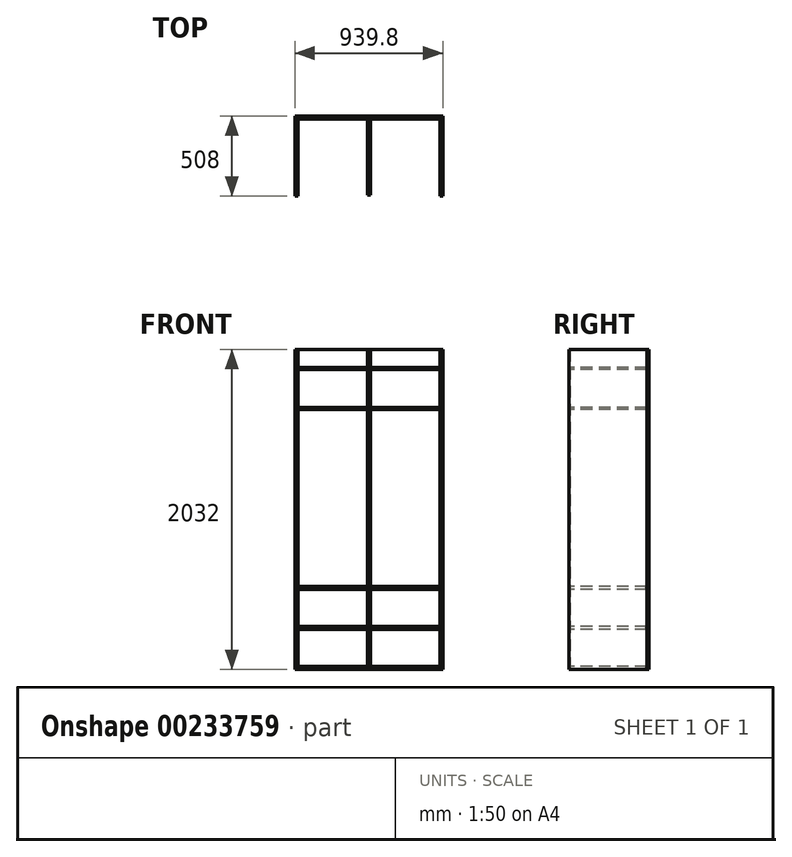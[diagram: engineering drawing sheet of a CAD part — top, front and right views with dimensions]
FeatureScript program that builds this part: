
annotation { "Feature Type Name" : "Feature", "Feature Type Description" : "" }
export const myFeature = defineFeature(function(context is Context, id is Id, definition is map)
    precondition{}
    {
        {
            var Q0;
            Q0=qCreatedBy(makeId("Front.planeOp"),FACE);
            var sketch = newSketch(context, id + "F0", { "sketchPlane" : qUnion([Q0])});
            skLineSegment(sketch, "E0.bottom", {"start": v(0, 0) * mm, "end": v(939.8, 0) * mm});
            skLineSegment(sketch, "E0.top", {"start": v(0, 2032) * mm, "end": v(939.8, 2032) * mm});
            skLineSegment(sketch, "E0.left", {"start": v(0, 0) * mm, "end": v(0, 2032) * mm});
            skLineSegment(sketch, "E0.right", {"start": v(939.8, 0) * mm, "end": v(939.8, 2032) * mm});
            skSolve(sketch);
        }
        {
            var Q0;
            Q0=makeQuery(id+"F0.imprint","IMPRINT",FACE,{"disambiguationData":[TD([[makeQuery(id+"F0.imprint","IMPRINT",EDGE,{"derivedFrom":sQuery(id+"F0.wireOp",EDGE,"E0.bottom")}),1.0]])]});
            extrude(context, id + "F1", {"entities" : qUnion([Q0]), "depth" : 19.05 * mm});
        }
        {
            var Q0;
            Q0=makeQuery(id+"F1.opExtrude","CAP_FACE",FACE,{"disambiguationData":[OSD([sQuery(id+"F0.wireOp",EDGE,"E0.bottom"),sQuery(id+"F0.wireOp",EDGE,"E0.top"),sQuery(id+"F0.wireOp",EDGE,"E0.left"),sQuery(id+"F0.wireOp",EDGE,"E0.right")])],"isStart":false});
            var sketch = newSketch(context, id + "F2", { "sketchPlane" : qUnion([Q0])});
            skLineSegment(sketch, "E1.bottom", {"start": v(0, 2032) * mm, "end": v(19.05, 2032) * mm});
            skLineSegment(sketch, "E1.top", {"start": v(0, 0) * mm, "end": v(19.05, 0) * mm});
            skLineSegment(sketch, "E1.left", {"start": v(0, 2032) * mm, "end": v(0, 0) * mm});
            skLineSegment(sketch, "E1.right", {"start": v(19.05, 2032) * mm, "end": v(19.05, 0) * mm});
            skLineSegment(sketch, "E2.bottom", {"start": v(939.8, 2032) * mm, "end": v(920.75, 2032) * mm});
            skLineSegment(sketch, "E2.top", {"start": v(939.8, 0) * mm, "end": v(920.75, 0) * mm});
            skLineSegment(sketch, "E2.left", {"start": v(939.8, 2032) * mm, "end": v(939.8, 0) * mm});
            skLineSegment(sketch, "E2.right", {"start": v(920.75, 2032) * mm, "end": v(920.75, 0) * mm});
            skLineSegment(sketch, "E3.bottom", {"start": v(469.9, 2032) * mm, "end": v(479.42, 2032) * mm});
            skLineSegment(sketch, "E3.top", {"start": v(469.9, 0) * mm, "end": v(479.42, 0) * mm});
            skLineSegment(sketch, "E3.right", {"start": v(479.42, 2032) * mm, "end": v(479.42, 0) * mm});
            skLineSegment(sketch, "E4.bottom", {"start": v(469.9, 2032) * mm, "end": v(460.37, 2032) * mm});
            skLineSegment(sketch, "E4.top", {"start": v(469.9, 0) * mm, "end": v(460.37, 0) * mm});
            skLineSegment(sketch, "E4.right", {"start": v(460.37, 2032) * mm, "end": v(460.37, 0) * mm});
            skSolve(sketch);
        }
        {
            var Q0;
            Q0 = qSketchRegion(id + "F2", true);
            extrude(context, id + "F3", {"entities" : qUnion([Q0]), "operationType" : NewBodyOperationType.REMOVE, "oppositeDirection" : true, "depth" : 6.35 * mm});
        }
        {
            var Q0;
            Q0=makeQuery(id+"F1.opExtrude","SWEPT_FACE",FACE,{"disambiguationData":[OSD([sQuery(id+"F0.wireOp",EDGE,"E0.right")])]});
            var sketch = newSketch(context, id + "F4", { "sketchPlane" : qUnion([Q0])});
            skLineSegment(sketch, "E5.bottom", {"start": v(-12.7, 2032) * mm, "end": v(-508, 2032) * mm});
            skLineSegment(sketch, "E5.top", {"start": v(-12.7, 0) * mm, "end": v(-508, 0) * mm});
            skLineSegment(sketch, "E5.left", {"start": v(-12.7, 2032) * mm, "end": v(-12.7, 0) * mm});
            skLineSegment(sketch, "E5.right", {"start": v(-508, 2032) * mm, "end": v(-508, 0) * mm});
            skSolve(sketch);
        }
        {
            var Q0;
            Q0=makeQuery(id+"F4.imprint","IMPRINT",FACE,{"disambiguationData":[TD([[makeQuery(id+"F4.imprint","IMPRINT",EDGE,{"derivedFrom":sQuery(id+"F4.wireOp",EDGE,"E5.bottom")}),1.0]])]});
            extrude(context, id + "F5", {"entities" : qUnion([Q0]), "oppositeDirection" : true, "depth" : 19.08 * mm});
        }
        {
            var Q0;
            Q0=makeQuery(id+"F1.opExtrude","SWEPT_FACE",FACE,{"disambiguationData":[OSD([sQuery(id+"F0.wireOp",EDGE,"E0.left")])]});
            var sketch = newSketch(context, id + "F6", { "sketchPlane" : qUnion([Q0])});
            skLineSegment(sketch, "E6.bottom", {"start": v(12.7, 2032) * mm, "end": v(508, 2032) * mm});
            skLineSegment(sketch, "E6.top", {"start": v(12.7, 0) * mm, "end": v(508, 0) * mm});
            skLineSegment(sketch, "E6.left", {"start": v(12.7, 2032) * mm, "end": v(12.7, 0) * mm});
            skLineSegment(sketch, "E6.right", {"start": v(508, 2032) * mm, "end": v(508, 0) * mm});
            skSolve(sketch);
        }
        {
            var Q0;
            Q0=makeQuery(id+"F6.imprint","IMPRINT",FACE,{"disambiguationData":[TD([[makeQuery(id+"F6.imprint","IMPRINT",EDGE,{"derivedFrom":sQuery(id+"F6.wireOp",EDGE,"E6.bottom")}),-1.0]])]});
            extrude(context, id + "F7", {"entities" : qUnion([Q0]), "oppositeDirection" : true, "depth" : 19.05 * mm});
        }
        {
            var Q0;
            Q0=makeQuery(id+"F3.boolean.opBoolean","COPY",FACE,{"derivedFrom":makeQuery(id+"F3.opExtrude","SWEPT_FACE",FACE,{"disambiguationData":[OSD([sQuery(id+"F2.wireOp",EDGE,"E3.right")])]})});
            var sketch = newSketch(context, id + "F8", { "sketchPlane" : qUnion([Q0])});
            skLineSegment(sketch, "E7.bottom", {"start": v(12.7, 2032) * mm, "end": v(501.65, 2032) * mm});
            skLineSegment(sketch, "E7.top", {"start": v(12.7, 0) * mm, "end": v(501.65, 0) * mm});
            skLineSegment(sketch, "E7.left", {"start": v(12.7, 2032) * mm, "end": v(12.7, 0) * mm});
            skLineSegment(sketch, "E7.right", {"start": v(501.65, 2032) * mm, "end": v(501.65, 0) * mm});
            skSolve(sketch);
        }
        {
            var Q0;
            Q0 = qSketchRegion(id + "F8", true);
            extrude(context, id + "F9", {"entities" : qUnion([Q0]), "depth" : 19.05 * mm});
        }
        {
            var Q0;
            {var subQ0=sQuery(id+"F0.wireOp",EDGE,"E0.bottom");var subQ1=sQuery(id+"F0.wireOp",EDGE,"E0.top");Q0=makeQuery(id+"F3.boolean.opBoolean","SPLIT",FACE,{"disambiguationData":[TD([makeQuery(id+"F3.opExtrude","SWEPT_FACE",FACE,{"disambiguationData":[OSD([sQuery(id+"F2.wireOp",EDGE,"E2.right")])]})])],"derivedFrom":makeQuery(id+"F1.opExtrude","CAP_FACE",FACE,{"disambiguationData":[OSD([subQ0,subQ1,sQuery(id+"F0.wireOp",EDGE,"E0.left"),sQuery(id+"F0.wireOp",EDGE,"E0.right")])],"isStart":false})});}
            var sketch = newSketch(context, id + "F10", { "sketchPlane" : qUnion([Q0])});
            skLineSegment(sketch, "E8.bottom", {"start": v(19.05, 0) * mm, "end": v(920.75, 0) * mm});
            skLineSegment(sketch, "E8.top", {"start": v(19.05, 19.05) * mm, "end": v(920.75, 19.05) * mm});
            skLineSegment(sketch, "E8.left", {"start": v(19.05, 0) * mm, "end": v(19.05, 19.05) * mm});
            skLineSegment(sketch, "E8.right", {"start": v(920.75, 0) * mm, "end": v(920.75, 19.05) * mm});
            skLineSegment(sketch, "E9.bottom", {"start": v(19.05, 254) * mm, "end": v(920.75, 254) * mm});
            skLineSegment(sketch, "E9.top", {"start": v(19.05, 273.05) * mm, "end": v(920.75, 273.05) * mm});
            skLineSegment(sketch, "E9.left", {"start": v(19.05, 254) * mm, "end": v(19.05, 273.05) * mm});
            skLineSegment(sketch, "E9.right", {"start": v(920.75, 254) * mm, "end": v(920.75, 273.05) * mm});
            skLineSegment(sketch, "E10.bottom", {"start": v(19.05, 508) * mm, "end": v(920.75, 508) * mm});
            skLineSegment(sketch, "E10.top", {"start": v(19.05, 527.05) * mm, "end": v(920.75, 527.05) * mm});
            skLineSegment(sketch, "E10.left", {"start": v(19.05, 508) * mm, "end": v(19.05, 527.05) * mm});
            skLineSegment(sketch, "E10.right", {"start": v(920.75, 508) * mm, "end": v(920.75, 527.05) * mm});
            skLineSegment(sketch, "E11.bottom", {"start": v(19.05, 1651) * mm, "end": v(920.75, 1651) * mm});
            skLineSegment(sketch, "E11.top", {"start": v(19.05, 1663.7) * mm, "end": v(920.75, 1663.7) * mm});
            skLineSegment(sketch, "E11.left", {"start": v(19.05, 1651) * mm, "end": v(19.05, 1663.7) * mm});
            skLineSegment(sketch, "E11.right", {"start": v(920.75, 1651) * mm, "end": v(920.75, 1663.7) * mm});
            skLineSegment(sketch, "E12.bottom", {"start": v(19.05, 1905) * mm, "end": v(920.75, 1905) * mm});
            skLineSegment(sketch, "E12.top", {"start": v(19.05, 1917.7) * mm, "end": v(920.75, 1917.7) * mm});
            skLineSegment(sketch, "E12.left", {"start": v(19.05, 1905) * mm, "end": v(19.05, 1917.7) * mm});
            skLineSegment(sketch, "E12.right", {"start": v(920.75, 1905) * mm, "end": v(920.75, 1917.7) * mm});
            skSolve(sketch);
        }
        {
            var Q0;
            Q0 = qSketchRegion(id + "F10", true);
            extrude(context, id + "F11", {"entities" : qUnion([Q0]), "operationType" : NewBodyOperationType.REMOVE, "oppositeDirection" : true, "depth" : 6.35 * mm});
        }
        {
            var Q0;
            Q0=makeQuery(id+"F7.opExtrude","CAP_FACE",FACE,{"disambiguationData":[OSD([sQuery(id+"F6.wireOp",EDGE,"E6.bottom"),sQuery(id+"F6.wireOp",EDGE,"E6.top"),sQuery(id+"F6.wireOp",EDGE,"E6.left"),sQuery(id+"F6.wireOp",EDGE,"E6.right")])],"isStart":false});
            var sketch = newSketch(context, id + "F12", { "sketchPlane" : qUnion([Q0])});
            skLineSegment(sketch, "E13.bottom", {"start": v(-12.7, 254) * mm, "end": v(-508, 254) * mm});
            skLineSegment(sketch, "E13.top", {"start": v(-12.7, 273.05) * mm, "end": v(-508, 273.05) * mm});
            skLineSegment(sketch, "E13.left", {"start": v(-12.7, 254) * mm, "end": v(-12.7, 273.05) * mm});
            skLineSegment(sketch, "E13.right", {"start": v(-508, 254) * mm, "end": v(-508, 273.05) * mm});
            skLineSegment(sketch, "E14.bottom", {"start": v(-12.7, 508) * mm, "end": v(-508, 508) * mm});
            skLineSegment(sketch, "E14.top", {"start": v(-12.7, 527.05) * mm, "end": v(-508, 527.05) * mm});
            skLineSegment(sketch, "E14.left", {"start": v(-12.7, 508) * mm, "end": v(-12.7, 527.05) * mm});
            skLineSegment(sketch, "E14.right", {"start": v(-508, 508) * mm, "end": v(-508, 527.05) * mm});
            skLineSegment(sketch, "E15.bottom", {"start": v(-12.7, 1905) * mm, "end": v(-508, 1905) * mm});
            skLineSegment(sketch, "E15.top", {"start": v(-12.7, 1917.7) * mm, "end": v(-508, 1917.7) * mm});
            skLineSegment(sketch, "E15.left", {"start": v(-12.7, 1905) * mm, "end": v(-12.7, 1917.7) * mm});
            skLineSegment(sketch, "E15.right", {"start": v(-508, 1905) * mm, "end": v(-508, 1917.7) * mm});
            skLineSegment(sketch, "E16.bottom", {"start": v(-12.7, 0) * mm, "end": v(-508, 0) * mm});
            skLineSegment(sketch, "E16.top", {"start": v(-12.7, 19.05) * mm, "end": v(-508, 19.05) * mm});
            skLineSegment(sketch, "E16.left", {"start": v(-12.7, 0) * mm, "end": v(-12.7, 19.05) * mm});
            skLineSegment(sketch, "E16.right", {"start": v(-508, 0) * mm, "end": v(-508, 19.05) * mm});
            skLineSegment(sketch, "E17.bottom", {"start": v(-12.7, 1651) * mm, "end": v(-508, 1651) * mm});
            skLineSegment(sketch, "E17.top", {"start": v(-12.7, 1663.7) * mm, "end": v(-508, 1663.7) * mm});
            skLineSegment(sketch, "E17.left", {"start": v(-12.7, 1651) * mm, "end": v(-12.7, 1663.7) * mm});
            skLineSegment(sketch, "E17.right", {"start": v(-508, 1651) * mm, "end": v(-508, 1663.7) * mm});
            skSolve(sketch);
        }
        {
            var Q0;
            Q0 = qSketchRegion(id + "F12", true);
            extrude(context, id + "F13", {"entities" : qUnion([Q0]), "operationType" : NewBodyOperationType.REMOVE, "oppositeDirection" : true, "depth" : 6.35 * mm});
        }
        {
            var Q0;
            Q0=makeQuery(id+"F5.opExtrude","CAP_FACE",FACE,{"disambiguationData":[OSD([sQuery(id+"F4.wireOp",EDGE,"E5.bottom"),sQuery(id+"F4.wireOp",EDGE,"E5.top"),sQuery(id+"F4.wireOp",EDGE,"E5.left"),sQuery(id+"F4.wireOp",EDGE,"E5.right")])],"isStart":false});
            var sketch = newSketch(context, id + "F14", { "sketchPlane" : qUnion([Q0])});
            skLineSegment(sketch, "E18.bottom", {"start": v(508, 1917.7) * mm, "end": v(12.7, 1917.7) * mm});
            skLineSegment(sketch, "E18.top", {"start": v(508, 1905) * mm, "end": v(12.7, 1905) * mm});
            skLineSegment(sketch, "E18.left", {"start": v(508, 1917.7) * mm, "end": v(508, 1905) * mm});
            skLineSegment(sketch, "E18.right", {"start": v(12.7, 1917.7) * mm, "end": v(12.7, 1905) * mm});
            skLineSegment(sketch, "E19.bottom", {"start": v(508, 1663.7) * mm, "end": v(12.7, 1663.7) * mm});
            skLineSegment(sketch, "E19.top", {"start": v(508, 1651) * mm, "end": v(12.7, 1651) * mm});
            skLineSegment(sketch, "E19.left", {"start": v(508, 1663.7) * mm, "end": v(508, 1651) * mm});
            skLineSegment(sketch, "E19.right", {"start": v(12.7, 1663.7) * mm, "end": v(12.7, 1651) * mm});
            skLineSegment(sketch, "E20.bottom", {"start": v(508, 527.05) * mm, "end": v(12.7, 527.05) * mm});
            skLineSegment(sketch, "E20.top", {"start": v(508, 508) * mm, "end": v(12.7, 508) * mm});
            skLineSegment(sketch, "E20.left", {"start": v(508, 527.05) * mm, "end": v(508, 508) * mm});
            skLineSegment(sketch, "E20.right", {"start": v(12.7, 527.05) * mm, "end": v(12.7, 508) * mm});
            skLineSegment(sketch, "E21.bottom", {"start": v(508, 273.05) * mm, "end": v(12.7, 273.05) * mm});
            skLineSegment(sketch, "E21.top", {"start": v(508, 254) * mm, "end": v(12.7, 254) * mm});
            skLineSegment(sketch, "E21.left", {"start": v(508, 273.05) * mm, "end": v(508, 254) * mm});
            skLineSegment(sketch, "E21.right", {"start": v(12.7, 273.05) * mm, "end": v(12.7, 254) * mm});
            skLineSegment(sketch, "E22.bottom", {"start": v(508, 19.05) * mm, "end": v(12.7, 19.05) * mm});
            skLineSegment(sketch, "E22.top", {"start": v(508, 0) * mm, "end": v(12.7, 0) * mm});
            skLineSegment(sketch, "E22.left", {"start": v(508, 19.05) * mm, "end": v(508, 0) * mm});
            skLineSegment(sketch, "E22.right", {"start": v(12.7, 19.05) * mm, "end": v(12.7, 0) * mm});
            skSolve(sketch);
        }
        {
            var Q0;
            Q0 = qSketchRegion(id + "F14", true);
            extrude(context, id + "F15", {"entities" : qUnion([Q0]), "operationType" : NewBodyOperationType.REMOVE, "oppositeDirection" : true, "depth" : 6.35 * mm});
        }
    });
